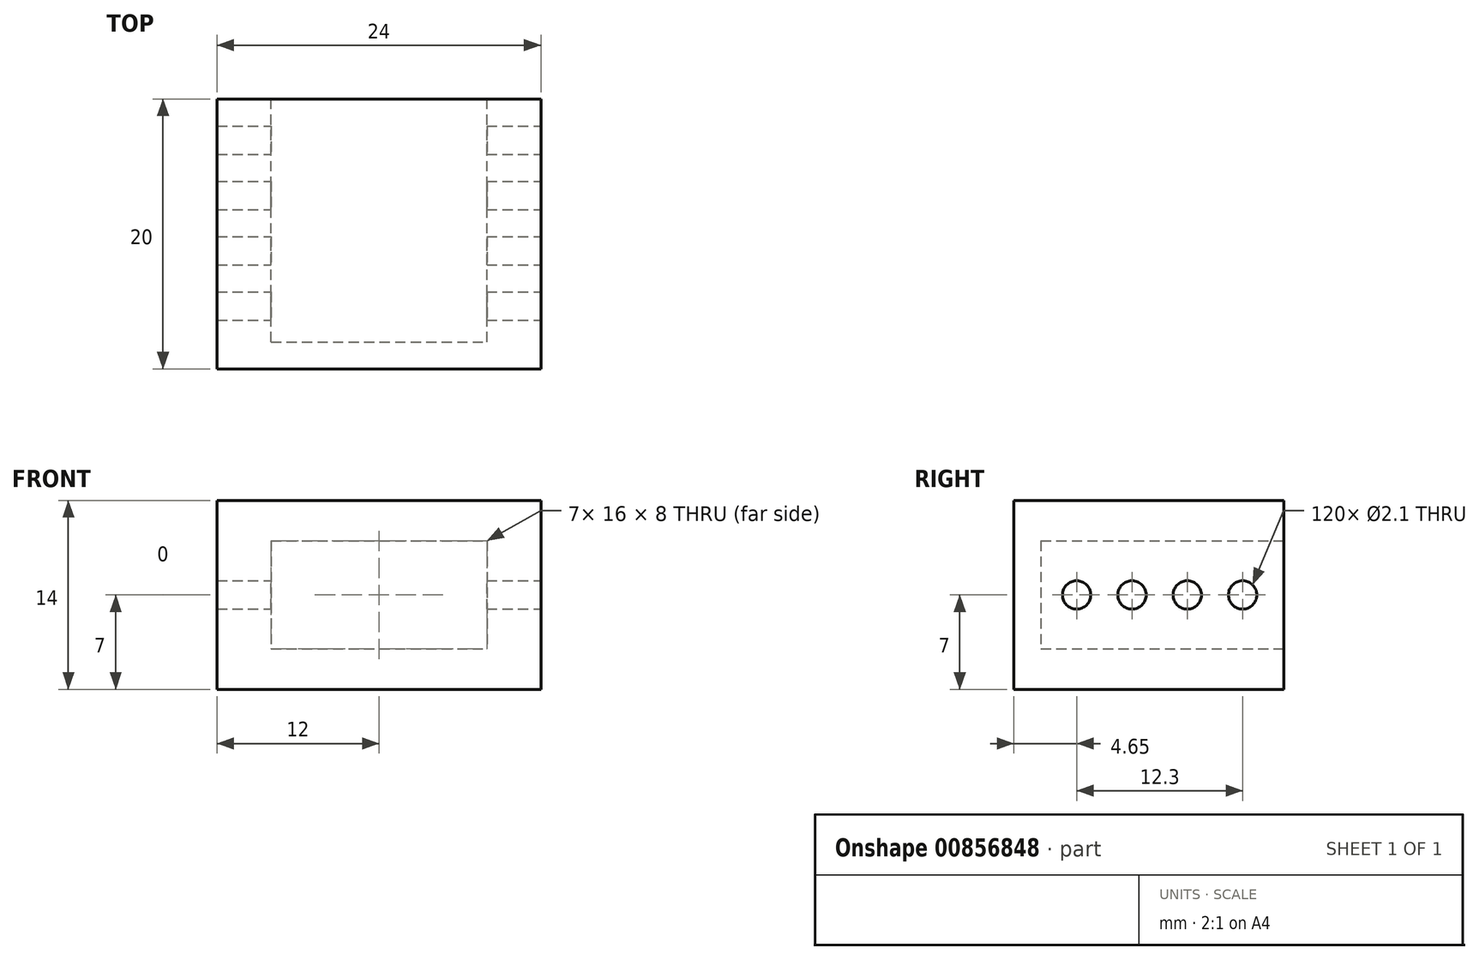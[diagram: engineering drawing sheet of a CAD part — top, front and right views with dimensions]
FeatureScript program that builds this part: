
annotation { "Feature Type Name" : "Feature", "Feature Type Description" : "" }
export const myFeature = defineFeature(function(context is Context, id is Id, definition is map)
    precondition{}
    {
        {
            var Q0;
            Q0=qCreatedBy(makeId("Front.planeOp"),FACE);
            var sketch = newSketch(context, id + "F0", { "sketchPlane" : qUnion([Q0])});
            skLineSegment(sketch, "E0.bottom", {"start": v(12, 7) * mm, "end": v(-12, 7) * mm});
            skLineSegment(sketch, "E0.top", {"start": v(12, -7) * mm, "end": v(-12, -7) * mm});
            skLineSegment(sketch, "E0.left", {"start": v(12, 7) * mm, "end": v(12, -7) * mm});
            skLineSegment(sketch, "E0.right", {"start": v(-12, 7) * mm, "end": v(-12, -7) * mm});
            skPoint(sketch, "E0.middle", {"position": v(0, 0) * mm});
            skSolve(sketch);
        }
        {
            var Q0;
            Q0=makeQuery(id+"F0.imprint","IMPRINT",FACE,{"disambiguationData":[TD([[makeQuery(id+"F0.imprint","IMPRINT",EDGE,{"derivedFrom":sQuery(id+"F0.wireOp",EDGE,"E0.bottom")}),1.0]])]});
            extrude(context, id + "F1", {"entities" : qUnion([Q0]), "depth" : 20 * mm, "offsetDistance" : 25 * mm});
        }
        {
            var Q0;
            Q0=makeQuery(id+"F1.opExtrude","CAP_FACE",FACE,{"disambiguationData":[OSD([sQuery(id+"F0.wireOp",EDGE,"E0.bottom"),sQuery(id+"F0.wireOp",EDGE,"E0.top"),sQuery(id+"F0.wireOp",EDGE,"E0.left"),sQuery(id+"F0.wireOp",EDGE,"E0.right")])],"isStart":true});
            var sketch = newSketch(context, id + "F2", { "sketchPlane" : qUnion([Q0])});
            skLineSegment(sketch, "E1.bottom", {"start": v(8, 4) * mm, "end": v(-8, 4) * mm});
            skLineSegment(sketch, "E1.top", {"start": v(8, -4) * mm, "end": v(-8, -4) * mm});
            skLineSegment(sketch, "E1.left", {"start": v(8, 4) * mm, "end": v(8, -4) * mm});
            skLineSegment(sketch, "E1.right", {"start": v(-8, 4) * mm, "end": v(-8, -4) * mm});
            skPoint(sketch, "E1.middle", {"position": v(0, 0) * mm});
            skSolve(sketch);
        }
        {
            var Q0;
            Q0 = qSketchRegion(id + "F2", true);
            extrude(context, id + "F3", {"entities" : qUnion([Q0]), "operationType" : NewBodyOperationType.REMOVE, "oppositeDirection" : true, "depth" : 18 * mm, "offsetDistance" : 25 * mm});
        }
        {
            var Q0;
            Q0=makeQuery(id+"F1.opExtrude","SWEPT_FACE",FACE,{"disambiguationData":[OSD([sQuery(id+"F0.wireOp",EDGE,"E0.left")])]});
            var sketch = newSketch(context, id + "F4", { "sketchPlane" : qUnion([Q0])});
            skLineSegment(sketch, "E2", {"start": v(-20, 0) * mm, "end": v(0, 0) * mm, "construction": true});
            skCircle(sketch, "E3", {"center": v(-15.35, 0) * mm, "radius": 1.05 * mm});
            skCircle(sketch, "E4", {"center": v(-11.25, 0) * mm, "radius": 1.05 * mm});
            skCircle(sketch, "E5", {"center": v(-3.05, 0) * mm, "radius": 1.05 * mm});
            skCircle(sketch, "E6", {"center": v(-7.15, 0) * mm, "radius": 1.05 * mm});
            skSolve(sketch);
        }
        {
            var Q0;
            Q0 = qSketchRegion(id + "F4", true);
            extrude(context, id + "F5", {"entities" : qUnion([Q0]), "operationType" : NewBodyOperationType.REMOVE, "endBound" : BoundingType.THROUGH_ALL, "oppositeDirection" : true, "depth" : 25 * mm, "offsetDistance" : 25 * mm});
        }
    });
